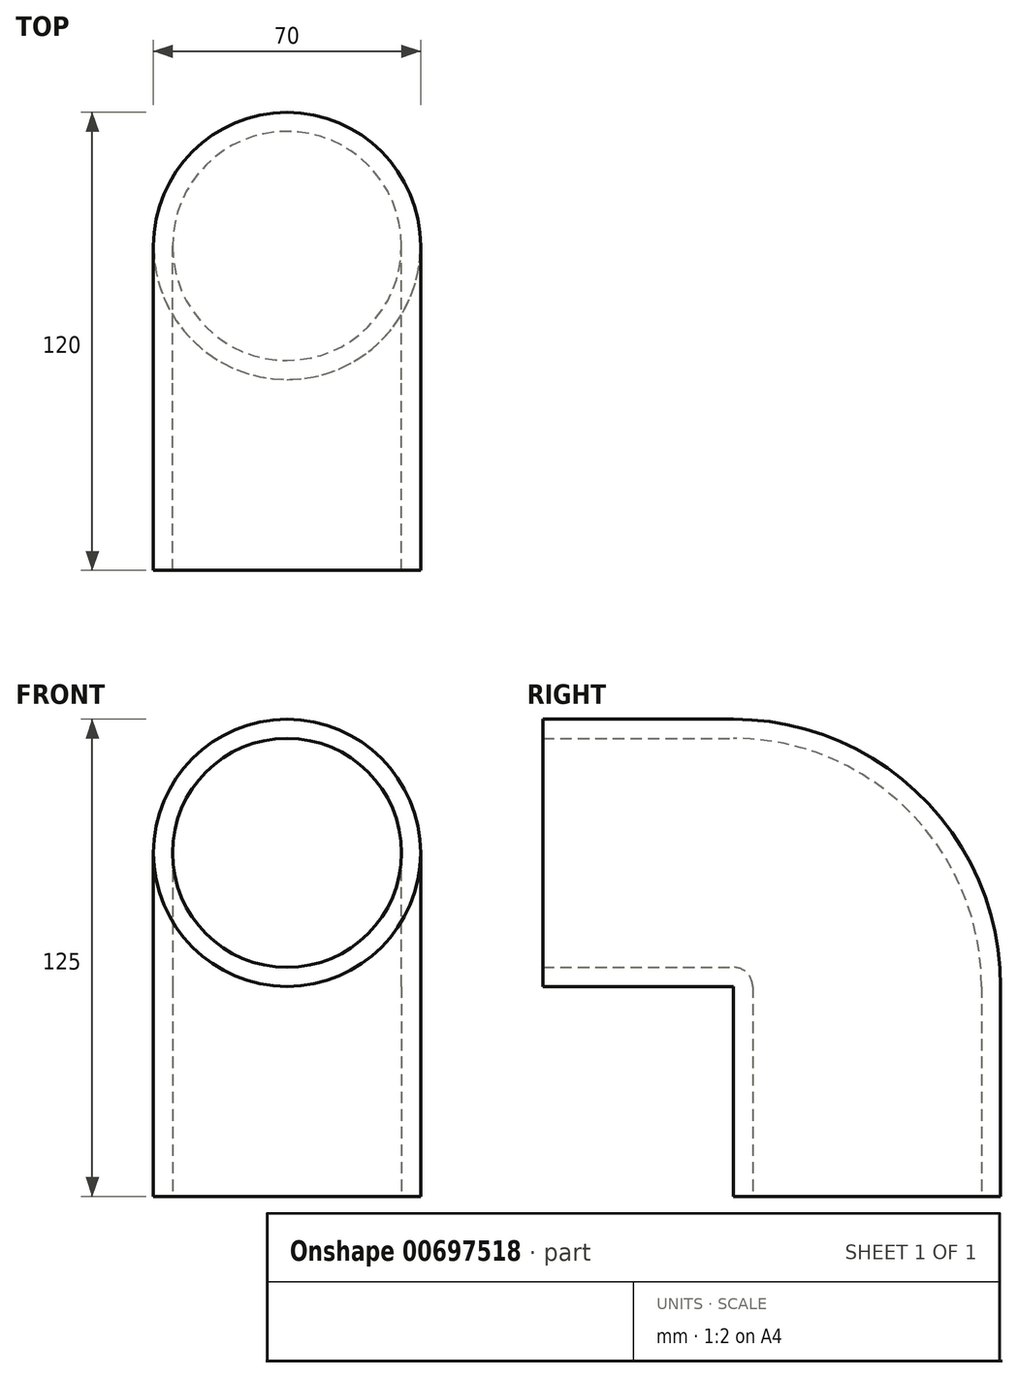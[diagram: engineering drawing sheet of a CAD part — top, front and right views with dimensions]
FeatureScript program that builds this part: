
annotation { "Feature Type Name" : "Feature", "Feature Type Description" : "" }
export const myFeature = defineFeature(function(context is Context, id is Id, definition is map)
    precondition{}
    {
        {
            var Q0;
            Q0=qCreatedBy(makeId("Front.planeOp"),FACE);
            var sketch = newSketch(context, id + "F0", { "sketchPlane" : qUnion([Q0])});
            skCircle(sketch, "E0", {"center": v(0, 0) * mm, "radius": 35 * mm});
            skSolve(sketch);
        }
        {
            var Q0;
            Q0=qCreatedBy(makeId("Top.planeOp"),FACE);
            cPlane(context, id + "F1", {"entities" : qUnion([Q0]), "cplaneType" : CPlaneType.OFFSET, "offset" : 90 * mm, "oppositeDirection" : true, "width" : 150 * mm, "height" : 150 * mm});
        }
        {
            var Q0;
            Q0=qCreatedBy(makeId("Right.planeOp"),FACE);
            var sketch = newSketch(context, id + "F2", { "sketchPlane" : qUnion([Q0])});
            skLineSegment(sketch, "E1", {"start": v(0, 0) * mm, "end": v(50, 0) * mm});
            skArc(sketch, "E2", {"start": v(85, -35) * mm, "mid": v(74.75, -10.25) * mm, "end": v(50, 0) * mm});
            skLineSegment(sketch, "E3", {"start": v(85, -35) * mm, "end": v(85, -90) * mm});
            skSolve(sketch);
        }
        {
            var Q0;
            Q0=qCreatedBy(id+"F1.planeOp",FACE);
            var sketch = newSketch(context, id + "F3", { "sketchPlane" : qUnion([Q0])});
            skCircle(sketch, "E4", {"center": v(0, 85) * mm, "radius": 35 * mm});
            skSolve(sketch);
        }
        {
            var Q0;
            Q0=makeQuery(id+"F0.imprint","IMPRINT",FACE,{"disambiguationData":[TD([[makeQuery(id+"F0.imprint","IMPRINT",EDGE,{"derivedFrom":sQuery(id+"F0.wireOp",EDGE,"E0")}),1.0]])]});
            var Q1;
            Q1=makeQuery(id+"F3.imprint","IMPRINT",FACE,{"disambiguationData":[TD([[makeQuery(id+"F3.imprint","IMPRINT",EDGE,{"derivedFrom":sQuery(id+"F3.wireOp",EDGE,"E4")}),1.0]])]});
            var Q2;
            Q2=sQuery(id+"F2.wireOp",EDGE,"E1");
            var Q3;
            Q3=sQuery(id+"F2.wireOp",EDGE,"E2");
            var Q4;
            Q4=sQuery(id+"F2.wireOp",EDGE,"E3");
            sweep(context, id + "F4", {"profiles" : qUnion([Q0, Q1]), "path" : qUnion([Q2, Q3, Q4])});
        }
        {
            var Q0;
            Q0=makeQuery(id+"F4.opSweep","CAP_FACE",FACE,{"disambiguationData":[OSD([sQuery(id+"F0.wireOp",EDGE,"E0"),sQuery(id+"F2.wireOp",VERTEX,"E1.start")])],"isStart":true});
            var Q1;
            Q1=makeQuery(id+"F4.opSweep","CAP_FACE",FACE,{"disambiguationData":[OSD([sQuery(id+"F0.wireOp",EDGE,"E0"),sQuery(id+"F2.wireOp",VERTEX,"E3.end")])],"isStart":false});
            shell(context, id + "F5", {"entities" : qUnion([Q0, Q1]), "thickness" : 5 * mm});
        }
        {
            var Q0;
            Q0=makeQuery(id+"F4.opSweep","SWEPT_BODY",BODY,{"disambiguationData":[OSD([sQuery(id+"F2.wireOp",EDGE,"E3"),sQuery(id+"F3.wireOp",EDGE,"E4")])]});
            deleteBodies(context, id + "F6", {"entities" : qUnion([Q0])});
        }
    });
